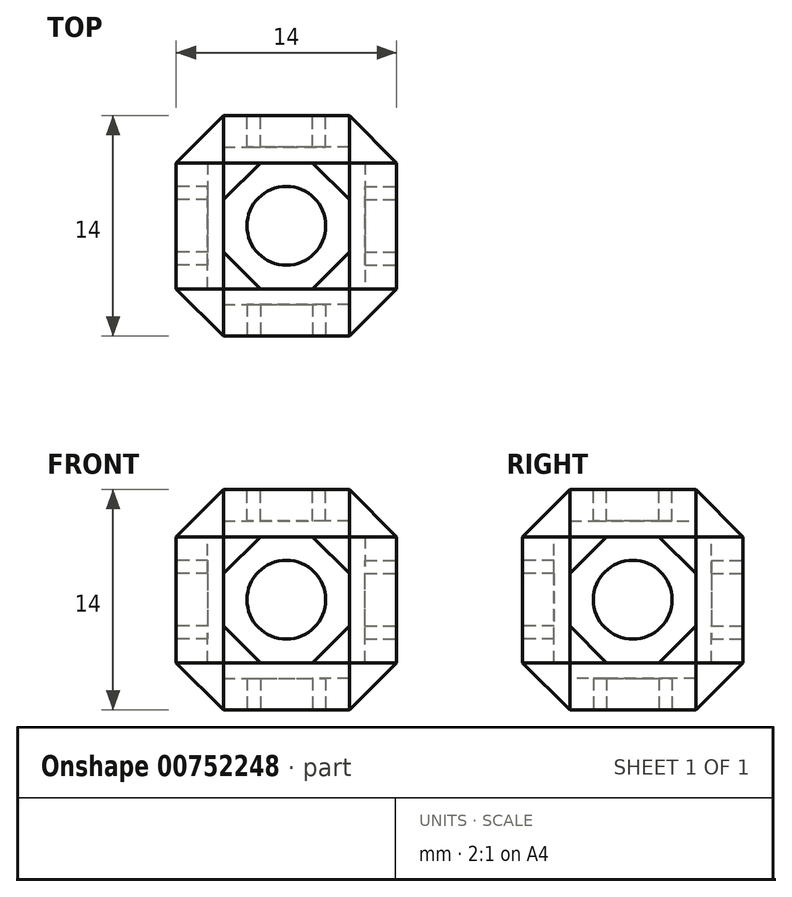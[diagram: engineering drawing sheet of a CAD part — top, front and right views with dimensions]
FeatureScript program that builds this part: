
annotation { "Feature Type Name" : "Feature", "Feature Type Description" : "" }
export const myFeature = defineFeature(function(context is Context, id is Id, definition is map)
    precondition{}
    {
        {
            var Q0;
            Q0=qCreatedBy(makeId("Top.planeOp"),FACE);
            var sketch = newSketch(context, id + "F0", { "sketchPlane" : qUnion([Q0])});
            skLineSegment(sketch, "E0.bottom", {"start": v(7, -7) * mm, "end": v(-7, -7) * mm});
            skLineSegment(sketch, "E0.top", {"start": v(7, 7) * mm, "end": v(-7, 7) * mm});
            skLineSegment(sketch, "E0.left", {"start": v(7, -7) * mm, "end": v(7, 7) * mm});
            skLineSegment(sketch, "E0.right", {"start": v(-7, -7) * mm, "end": v(-7, 7) * mm});
            skPoint(sketch, "E0.middle", {"position": v(0, 0) * mm});
            skSolve(sketch);
        }
        {
            var Q0;
            Q0=makeQuery(id+"F0.imprint","IMPRINT",FACE,{"disambiguationData":[TD([[makeQuery(id+"F0.imprint","IMPRINT",EDGE,{"derivedFrom":sQuery(id+"F0.wireOp",EDGE,"E0.bottom")}),-1.0]])]});
            extrude(context, id + "F1", {"entities" : qUnion([Q0]), "endBound" : BoundingType.SYMMETRIC, "depth" : 14 * mm, "offsetDistance" : 25 * mm});
        }
        {
            var Q0;
            Q0=makeQuery(id+"F1.opExtrude","SWEPT_FACE",FACE,{"disambiguationData":[OSD([sQuery(id+"F0.wireOp",EDGE,"E0.left")])]});
            var sketch = newSketch(context, id + "F2", { "sketchPlane" : qUnion([Q0])});
            skCircle(sketch, "E1.cCircle", {"center": v(0, 0) * mm, "radius": 4 * mm, "construction": true});
            skLineSegment(sketch, "E1.0", {"start": v(-4, -1.66) * mm, "end": v(-4, 1.66) * mm});
            skLineSegment(sketch, "E1.1", {"start": v(-4, 1.66) * mm, "end": v(-1.66, 4) * mm});
            skLineSegment(sketch, "E1.2", {"start": v(-1.66, 4) * mm, "end": v(1.66, 4) * mm});
            skLineSegment(sketch, "E1.3", {"start": v(1.66, 4) * mm, "end": v(4, 1.66) * mm});
            skLineSegment(sketch, "E1.4", {"start": v(4, 1.66) * mm, "end": v(4, -1.66) * mm});
            skLineSegment(sketch, "E1.5", {"start": v(4, -1.66) * mm, "end": v(1.66, -4) * mm});
            skLineSegment(sketch, "E1.6", {"start": v(1.66, -4) * mm, "end": v(-1.66, -4) * mm});
            skLineSegment(sketch, "E1.7", {"start": v(-1.66, -4) * mm, "end": v(-4, -1.66) * mm});
            skPoint(sketch, "E1.0.midPoint", {"position": v(-4, 0) * mm});
            skCircle(sketch, "E2", {"center": v(0, 0) * mm, "radius": 2.5 * mm});
            skSolve(sketch);
        }
        {
            var Q0;
            Q0=qCreatedBy(makeId("Front.planeOp"),FACE);
            var sketch = newSketch(context, id + "F3", { "sketchPlane" : qUnion([Q0])});
            skLineSegment(sketch, "E3", {"start": v(0, 0) * mm, "end": v(0, -10.81) * mm});
            skLineSegment(sketch, "E4", {"start": v(0, 0) * mm, "end": v(-9.79, 0) * mm});
            skSolve(sketch);
        }
        {
            var Q0;
            Q0=qSketchRegion(id+"F2",true);
            extrude(context, id + "F4", {"entities" : qUnion([Q0]), "operationType" : NewBodyOperationType.REMOVE, "oppositeDirection" : true, "depth" : 2 * mm, "offsetDistance" : 25 * mm});
        }
        {
            var Q0;
            Q0=makeQuery(id+"F1.opExtrude","SWEPT_FACE",FACE,{"disambiguationData":[OSD([sQuery(id+"F0.wireOp",EDGE,"E0.top")])]});
            var Q1;
            Q1=makeQuery(id+"F1.opExtrude","CAP_FACE",FACE,{"disambiguationData":[OSD([sQuery(id+"F0.wireOp",EDGE,"E0.bottom"),sQuery(id+"F0.wireOp",EDGE,"E0.top"),sQuery(id+"F0.wireOp",EDGE,"E0.left"),sQuery(id+"F0.wireOp",EDGE,"E0.right")])],"isStart":false});
            var Q2;
            Q2=makeQuery(id+"F1.opExtrude","SWEPT_FACE",FACE,{"disambiguationData":[OSD([sQuery(id+"F0.wireOp",EDGE,"E0.bottom")])]});
            var Q3;
            Q3=makeQuery(id+"F1.opExtrude","CAP_FACE",FACE,{"disambiguationData":[OSD([sQuery(id+"F0.wireOp",EDGE,"E0.bottom"),sQuery(id+"F0.wireOp",EDGE,"E0.top"),sQuery(id+"F0.wireOp",EDGE,"E0.left"),sQuery(id+"F0.wireOp",EDGE,"E0.right")])],"isStart":true});
            chamfer(context, id + "F5", {"entities" : qUnion([Q0, Q1, Q2, Q3]), "width" : 3 * mm, "tangentPropagation" : true});
        }
        {
            var Q0;
            Q0=makeQuery(id+"F1.opExtrude","SWEPT_FACE",FACE,{"disambiguationData":[OSD([sQuery(id+"F0.wireOp",EDGE,"E0.top")])]});
            var sketch = newSketch(context, id + "F6", { "sketchPlane" : qUnion([Q0])});
            skCircle(sketch, "E5.cCircle", {"center": v(0, 0) * mm, "radius": 4 * mm, "construction": true});
            skLineSegment(sketch, "E5.0", {"start": v(-4, -1.66) * mm, "end": v(-4, 1.66) * mm});
            skLineSegment(sketch, "E5.1", {"start": v(-4, 1.66) * mm, "end": v(-1.66, 4) * mm});
            skLineSegment(sketch, "E5.2", {"start": v(-1.66, 4) * mm, "end": v(1.66, 4) * mm});
            skLineSegment(sketch, "E5.3", {"start": v(1.66, 4) * mm, "end": v(4, 1.66) * mm});
            skLineSegment(sketch, "E5.4", {"start": v(4, 1.66) * mm, "end": v(4, -1.66) * mm});
            skLineSegment(sketch, "E5.5", {"start": v(4, -1.66) * mm, "end": v(1.66, -4) * mm});
            skLineSegment(sketch, "E5.6", {"start": v(1.66, -4) * mm, "end": v(-1.66, -4) * mm});
            skLineSegment(sketch, "E5.7", {"start": v(-1.66, -4) * mm, "end": v(-4, -1.66) * mm});
            skPoint(sketch, "E5.0.midPoint", {"position": v(-4, 0) * mm});
            skCircle(sketch, "E6", {"center": v(0, 0) * mm, "radius": 2.5 * mm});
            skSolve(sketch);
        }
        {
            var Q0;
            Q0=makeQuery(id+"F1.opExtrude","CAP_FACE",FACE,{"disambiguationData":[OSD([sQuery(id+"F0.wireOp",EDGE,"E0.bottom"),sQuery(id+"F0.wireOp",EDGE,"E0.top"),sQuery(id+"F0.wireOp",EDGE,"E0.left"),sQuery(id+"F0.wireOp",EDGE,"E0.right")])],"isStart":false});
            var sketch = newSketch(context, id + "F7", { "sketchPlane" : qUnion([Q0])});
            skCircle(sketch, "E7.cCircle", {"center": v(0, 0) * mm, "radius": 4 * mm, "construction": true});
            skLineSegment(sketch, "E7.0", {"start": v(-4, -1.66) * mm, "end": v(-4, 1.66) * mm});
            skLineSegment(sketch, "E7.1", {"start": v(-4, 1.66) * mm, "end": v(-1.66, 4) * mm});
            skLineSegment(sketch, "E7.2", {"start": v(-1.66, 4) * mm, "end": v(1.66, 4) * mm});
            skLineSegment(sketch, "E7.3", {"start": v(1.66, 4) * mm, "end": v(4, 1.66) * mm});
            skLineSegment(sketch, "E7.4", {"start": v(4, 1.66) * mm, "end": v(4, -1.66) * mm});
            skLineSegment(sketch, "E7.5", {"start": v(4, -1.66) * mm, "end": v(1.66, -4) * mm});
            skLineSegment(sketch, "E7.6", {"start": v(1.66, -4) * mm, "end": v(-1.66, -4) * mm});
            skLineSegment(sketch, "E7.7", {"start": v(-1.66, -4) * mm, "end": v(-4, -1.66) * mm});
            skPoint(sketch, "E7.0.midPoint", {"position": v(-4, 0) * mm});
            skCircle(sketch, "E8", {"center": v(0, 0) * mm, "radius": 2.5 * mm});
            skSolve(sketch);
        }
        {
            var Q0;
            Q0=makeQuery(id+"F1.opExtrude","SWEPT_FACE",FACE,{"disambiguationData":[OSD([sQuery(id+"F0.wireOp",EDGE,"E0.right")])]});
            var sketch = newSketch(context, id + "F8", { "sketchPlane" : qUnion([Q0])});
            skCircle(sketch, "E9.cCircle", {"center": v(0, 0) * mm, "radius": 4 * mm, "construction": true});
            skLineSegment(sketch, "E9.0", {"start": v(-4, -1.66) * mm, "end": v(-4, 1.66) * mm});
            skLineSegment(sketch, "E9.1", {"start": v(-4, 1.66) * mm, "end": v(-1.66, 4) * mm});
            skLineSegment(sketch, "E9.2", {"start": v(-1.66, 4) * mm, "end": v(1.66, 4) * mm});
            skLineSegment(sketch, "E9.3", {"start": v(1.66, 4) * mm, "end": v(4, 1.66) * mm});
            skLineSegment(sketch, "E9.4", {"start": v(4, 1.66) * mm, "end": v(4, -1.66) * mm});
            skLineSegment(sketch, "E9.5", {"start": v(4, -1.66) * mm, "end": v(1.66, -4) * mm});
            skLineSegment(sketch, "E9.6", {"start": v(1.66, -4) * mm, "end": v(-1.66, -4) * mm});
            skLineSegment(sketch, "E9.7", {"start": v(-1.66, -4) * mm, "end": v(-4, -1.66) * mm});
            skPoint(sketch, "E9.0.midPoint", {"position": v(-4, 0) * mm});
            skCircle(sketch, "E10", {"center": v(0, 0) * mm, "radius": 2.5 * mm});
            skSolve(sketch);
        }
        {
            var Q0;
            Q0=makeQuery(id+"F1.opExtrude","SWEPT_FACE",FACE,{"disambiguationData":[OSD([sQuery(id+"F0.wireOp",EDGE,"E0.bottom")])]});
            var sketch = newSketch(context, id + "F9", { "sketchPlane" : qUnion([Q0])});
            skCircle(sketch, "E11.cCircle", {"center": v(0, 0) * mm, "radius": 4 * mm, "construction": true});
            skLineSegment(sketch, "E11.0", {"start": v(-4, -1.66) * mm, "end": v(-4, 1.66) * mm});
            skLineSegment(sketch, "E11.1", {"start": v(-4, 1.66) * mm, "end": v(-1.66, 4) * mm});
            skLineSegment(sketch, "E11.2", {"start": v(-1.66, 4) * mm, "end": v(1.66, 4) * mm});
            skLineSegment(sketch, "E11.3", {"start": v(1.66, 4) * mm, "end": v(4, 1.66) * mm});
            skLineSegment(sketch, "E11.4", {"start": v(4, 1.66) * mm, "end": v(4, -1.66) * mm});
            skLineSegment(sketch, "E11.5", {"start": v(4, -1.66) * mm, "end": v(1.66, -4) * mm});
            skLineSegment(sketch, "E11.6", {"start": v(1.66, -4) * mm, "end": v(-1.66, -4) * mm});
            skLineSegment(sketch, "E11.7", {"start": v(-1.66, -4) * mm, "end": v(-4, -1.66) * mm});
            skPoint(sketch, "E11.0.midPoint", {"position": v(-4, 0) * mm});
            skCircle(sketch, "E12", {"center": v(0, 0) * mm, "radius": 2.5 * mm});
            skSolve(sketch);
        }
        {
            var Q0;
            Q0=makeQuery(id+"F1.opExtrude","CAP_FACE",FACE,{"disambiguationData":[OSD([sQuery(id+"F0.wireOp",EDGE,"E0.bottom"),sQuery(id+"F0.wireOp",EDGE,"E0.top"),sQuery(id+"F0.wireOp",EDGE,"E0.left"),sQuery(id+"F0.wireOp",EDGE,"E0.right")])],"isStart":true});
            var sketch = newSketch(context, id + "F10", { "sketchPlane" : qUnion([Q0])});
            skCircle(sketch, "E13.cCircle", {"center": v(0, 0) * mm, "radius": 4 * mm, "construction": true});
            skLineSegment(sketch, "E13.0", {"start": v(-4, -1.66) * mm, "end": v(-4, 1.66) * mm});
            skLineSegment(sketch, "E13.1", {"start": v(-4, 1.66) * mm, "end": v(-1.66, 4) * mm});
            skLineSegment(sketch, "E13.2", {"start": v(-1.66, 4) * mm, "end": v(1.66, 4) * mm});
            skLineSegment(sketch, "E13.3", {"start": v(1.66, 4) * mm, "end": v(4, 1.66) * mm});
            skLineSegment(sketch, "E13.4", {"start": v(4, 1.66) * mm, "end": v(4, -1.66) * mm});
            skLineSegment(sketch, "E13.5", {"start": v(4, -1.66) * mm, "end": v(1.66, -4) * mm});
            skLineSegment(sketch, "E13.6", {"start": v(1.66, -4) * mm, "end": v(-1.66, -4) * mm});
            skLineSegment(sketch, "E13.7", {"start": v(-1.66, -4) * mm, "end": v(-4, -1.66) * mm});
            skPoint(sketch, "E13.0.midPoint", {"position": v(-4, 0) * mm});
            skCircle(sketch, "E14", {"center": v(0, 0) * mm, "radius": 2.5 * mm});
            skSolve(sketch);
        }
        {
            var Q0;
            Q0=qSketchRegion(id+"F6",true);
            extrude(context, id + "F11", {"entities" : qUnion([Q0]), "operationType" : NewBodyOperationType.REMOVE, "oppositeDirection" : true, "depth" : 2 * mm, "offsetDistance" : 25 * mm});
        }
        {
            var Q0;
            Q0=qSketchRegion(id+"F7",true);
            extrude(context, id + "F12", {"entities" : qUnion([Q0]), "operationType" : NewBodyOperationType.REMOVE, "oppositeDirection" : true, "depth" : 2 * mm, "offsetDistance" : 25 * mm});
        }
        {
            var Q0;
            Q0=qSketchRegion(id+"F8",true);
            extrude(context, id + "F13", {"entities" : qUnion([Q0]), "operationType" : NewBodyOperationType.REMOVE, "oppositeDirection" : true, "depth" : 2 * mm, "offsetDistance" : 25 * mm});
        }
        {
            var Q0;
            Q0=qSketchRegion(id+"F9",true);
            extrude(context, id + "F14", {"entities" : qUnion([Q0]), "operationType" : NewBodyOperationType.REMOVE, "oppositeDirection" : true, "depth" : 2 * mm, "offsetDistance" : 25 * mm});
        }
        {
            var Q0;
            Q0=qSketchRegion(id+"F10",true);
            extrude(context, id + "F15", {"entities" : qUnion([Q0]), "operationType" : NewBodyOperationType.REMOVE, "oppositeDirection" : true, "depth" : 2 * mm, "offsetDistance" : 25 * mm});
        }
    });
